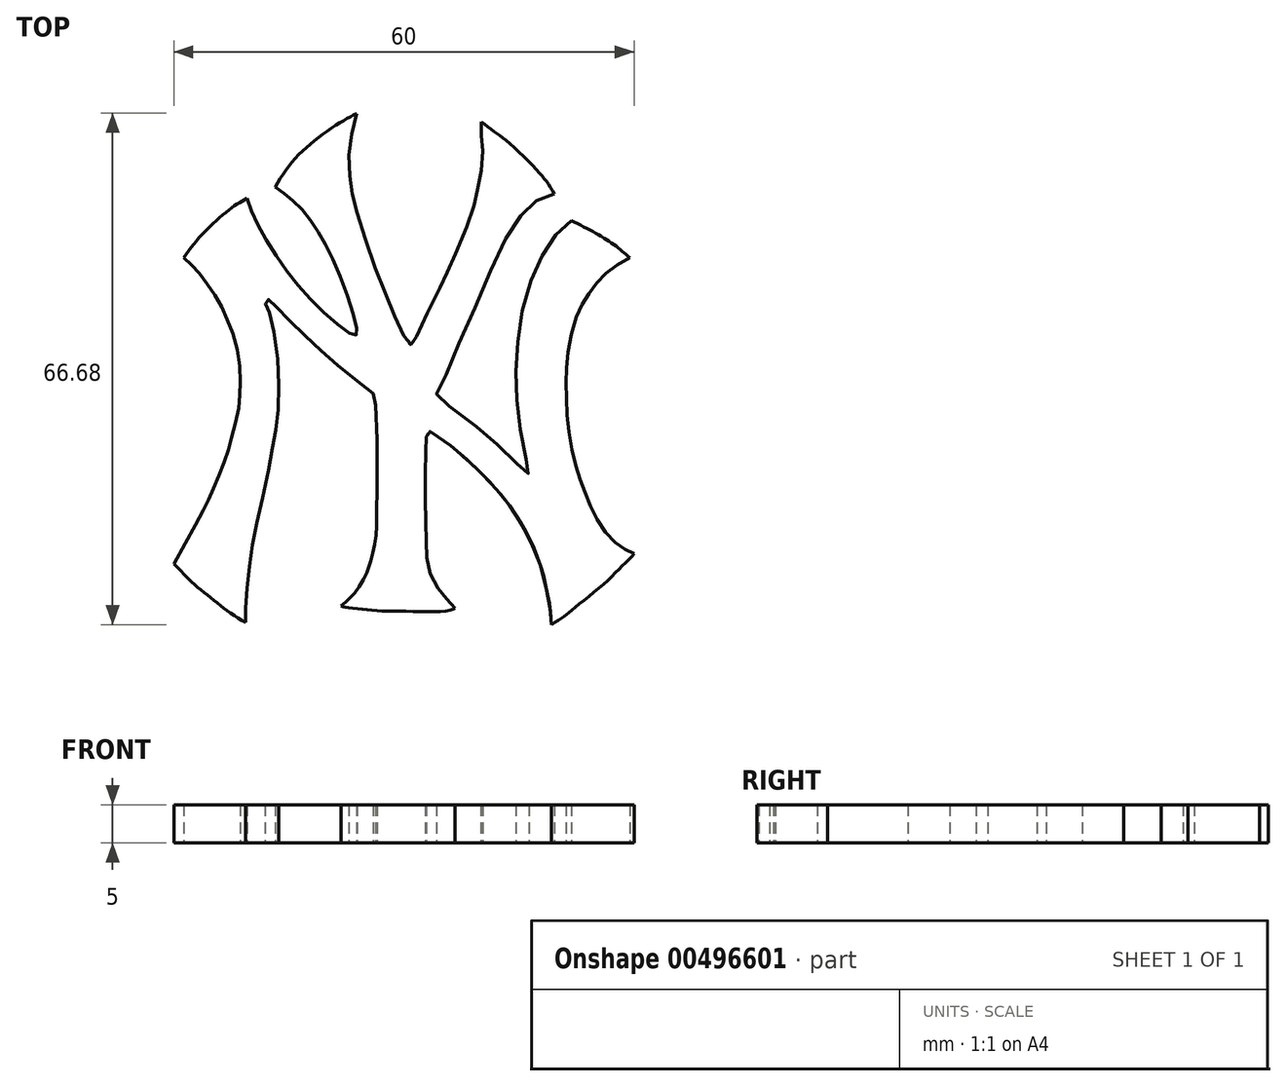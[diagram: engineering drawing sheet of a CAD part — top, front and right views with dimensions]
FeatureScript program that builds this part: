
annotation { "Feature Type Name" : "Feature", "Feature Type Description" : "" }
export const myFeature = defineFeature(function(context is Context, id is Id, definition is map)
    precondition{}
    {
        {
            var Q0;
            Q0=qCreatedBy(makeId("Top.planeOp"),FACE);
            var sketch = newSketch(context, id + "F0", { "sketchPlane" : qUnion([Q0])});
            skFitSpline(sketch, "E0", {"points": [v(-20.6, 24.51) * mm, v(-21.8, 23.88) * mm, v(-23.3, 22.78) * mm, v(-25.43, 20.88) * mm, v(-27.16, 19.06) * mm, v(-28.9, 16.77) * mm], "startDerivative": vector(-7.62, -3.74) * mm, "endDerivative": vector(-7.65, -10.58) * mm});
            skFitSpline(sketch, "E1", {"points": [v(-28.9, 16.77) * mm, v(-27.48, 15.5) * mm, v(-25.98, 13.53) * mm, v(-24.24, 11) * mm, v(-22.98, 8.16) * mm, v(-21.71, 3.97) * mm, v(-21.55, 0) * mm, v(-21.71, -2.67) * mm, v(-22.58, -6.46) * mm, v(-23.21, -8.83) * mm, v(-24.48, -12) * mm, v(-25.5, -14.44) * mm, v(-26.7, -16.81) * mm, v(-30.17, -23.14) * mm], "startDerivative": vector(24.88, -19.82) * mm, "endDerivative": vector(-34.53, -62.2) * mm});
            skFitSpline(sketch, "E2", {"points": [v(-30.17, -23.14) * mm, v(-28.9, -24.47) * mm, v(-27.36, -25.97) * mm, v(-25.27, -27.63) * mm, v(-23.21, -29.25) * mm, v(-20.84, -30.8) * mm], "startDerivative": vector(7.12, -7.55) * mm, "endDerivative": vector(11.27, -6.93) * mm});
            skFitSpline(sketch, "E3", {"points": [v(-20.84, -30.8) * mm, v(-20.84, -28.86) * mm, v(-20.49, -25.02) * mm, v(-19.93, -20.68) * mm, v(-18.87, -15.74) * mm, v(-17.52, -9.22) * mm, v(-16.96, -6.01) * mm, v(-16.51, -1.88) * mm, v(-16.74, 4.38) * mm, v(-17.63, 9.4) * mm, v(-18.07, 10.37) * mm, v(-18.27, 11.01) * mm, v(-18.07, 11.35) * mm, v(-17.68, 11.27) * mm, v(-16.9, 10.43) * mm, v(-14.53, 8) * mm, v(-11.31, 4.92) * mm, v(-7.93, 2.02) * mm, v(-4.22, -0.92) * mm], "startDerivative": vector(-1.2, 39.83) * mm, "endDerivative": vector(54.21, -42.15) * mm});
            skFitSpline(sketch, "E4", {"points": [v(-4.22, -0.92) * mm, v(-3.85, -2.48) * mm], "startDerivative": vector(0.36, -1.56) * mm, "endDerivative": vector(0.36, -1.56) * mm});
            skFitSpline(sketch, "E5", {"points": [v(-3.85, -2.48) * mm, v(-3.66, -8.07) * mm, v(-3.7, -15) * mm, v(-3.72, -16.94) * mm, v(-3.85, -19.64) * mm, v(-4.5, -22.63) * mm, v(-4.94, -24.05) * mm, v(-6.07, -26.2) * mm, v(-7.38, -27.78) * mm, v(-8.37, -28.62) * mm], "startDerivative": vector(1.65, -32.98) * mm, "endDerivative": vector(-12.84, -10.3) * mm});
            skFitSpline(sketch, "E6", {"points": [v(-8.37, -28.62) * mm, v(-7.9, -28.81) * mm, v(-6.02, -29) * mm, v(-3.29, -29.27) * mm, v(0.79, -29.34) * mm, v(5.5, -29.26) * mm, v(6.51, -28.9) * mm], "startDerivative": vector(4.84, -2.6) * mm, "endDerivative": vector(6.8, 3.5) * mm});
            skFitSpline(sketch, "E7", {"points": [v(6.51, -28.9) * mm, v(5.6, -27.93) * mm, v(4.49, -26.66) * mm, v(3.35, -24.62) * mm, v(2.78, -22.22) * mm, v(2.73, -19.85) * mm, v(2.64, -16.02) * mm, v(2.64, -10.53) * mm, v(2.73, -7.14) * mm, v(2.84, -6.23) * mm, v(3.05, -5.91) * mm, v(3.4, -5.92) * mm, v(4.07, -6.44) * mm, v(5.65, -7.56) * mm, v(8.76, -10.22) * mm, v(11.63, -13.12) * mm, v(13.92, -16.04) * mm, v(16.13, -19.75) * mm, v(17.87, -24.18) * mm, v(18.82, -28.62) * mm, v(19.08, -31.06) * mm], "startDerivative": vector(-24.2, 26.34) * mm, "endDerivative": vector(3.79, -45.4) * mm});
            skFitSpline(sketch, "E8", {"points": [v(19.08, -31.06) * mm, v(20.64, -30.08) * mm, v(21.79, -29.13) * mm, v(25.36, -26.22) * mm, v(28.14, -23.58) * mm, v(29.83, -21.85) * mm], "startDerivative": vector(10.32, 6.05) * mm, "endDerivative": vector(8.55, 8.85) * mm});
            skFitSpline(sketch, "E9", {"points": [v(29.83, -21.85) * mm, v(28, -20.81) * mm, v(25.55, -18.27) * mm, v(23.67, -14.37) * mm, v(22.44, -11) * mm, v(21.3, -5.78) * mm, v(20.98, -0.57) * mm, v(21.14, 3.66) * mm, v(22.4, 9.31) * mm, v(23.98, 12.12) * mm, v(26.1, 14.72) * mm, v(29.3, 16.77) * mm], "startDerivative": vector(-27.08, 13.1) * mm, "endDerivative": vector(38.6, 20.7) * mm});
            skFitSpline(sketch, "E10", {"points": [v(29.3, 16.77) * mm, v(26.5, 18.98) * mm, v(21.65, 21.64) * mm], "startDerivative": vector(-5.75, 5) * mm, "endDerivative": vector(-9.43, 4.75) * mm});
            skFitSpline(sketch, "E11", {"points": [v(21.65, 21.64) * mm, v(20.18, 20.38) * mm, v(18.52, 18.19) * mm, v(17.1, 15.5) * mm, v(15.7, 11.64) * mm, v(14.8, 7.06) * mm, v(14.44, 2.77) * mm, v(14.5, -0.92) * mm, v(14.9, -4.82) * mm, v(15.7, -9.28) * mm, v(16.1, -10.8) * mm, v(16.08, -11.33) * mm, v(15.63, -11.3) * mm, v(14.67, -10.2) * mm, v(12.25, -7.8) * mm, v(9.76, -5.66) * mm, v(5.62, -2.48) * mm, v(4.14, -1.25) * mm, v(4.1, -0.92) * mm, v(5.01, 0.94) * mm, v(7, 5.6) * mm, v(9.88, 12.12) * mm, v(12.56, 18.3) * mm, v(14.62, 21.64) * mm, v(16.32, 23.6) * mm, v(17.78, 24.58) * mm, v(19.44, 25.13) * mm], "startDerivative": vector(-46.4, -35.94) * mm, "endDerivative": vector(56.95, 15.73) * mm});
            skFitSpline(sketch, "E12", {"points": [v(19.44, 25.13) * mm, v(18.42, 26.71) * mm, v(16.98, 28.4) * mm, v(13.34, 31.95) * mm, v(11.7, 33.18) * mm, v(9.9, 34.49) * mm], "startDerivative": vector(-5.86, 9.59) * mm, "endDerivative": vector(-10.1, 7.52) * mm});
            skFitSpline(sketch, "E13", {"points": [v(9.9, 34.49) * mm, v(9.9, 32.59) * mm, v(10.08, 29.67) * mm, v(9.38, 25.47) * mm, v(8.7, 22.65) * mm, v(5.86, 15.8) * mm, v(4.7, 13.28) * mm, v(1.44, 6.53) * mm, v(0.85, 5.52) * mm, v(0.46, 5.6) * mm, v(-1.1, 8.6) * mm, v(-3.72, 14.91) * mm, v(-6.41, 23.04) * mm, v(-7.14, 26.59) * mm, v(-7.28, 31.03) * mm, v(-6.37, 35.62) * mm], "startDerivative": vector(-1.6, -38.96) * mm, "endDerivative": vector(15.71, 61.1) * mm});
            skFitSpline(sketch, "E14", {"points": [v(-6.37, 35.62) * mm, v(-8.37, 34.49) * mm, v(-11.7, 32.15) * mm, v(-14.77, 29.25) * mm, v(-16.95, 26) * mm], "startDerivative": vector(-9.36, -5) * mm, "endDerivative": vector(-7.7, -12.78) * mm});
            skFitSpline(sketch, "E15", {"points": [v(-16.95, 26) * mm, v(-15.11, 24.6) * mm, v(-12.88, 22.37) * mm, v(-10.8, 19.19) * mm, v(-8.37, 14.05) * mm, v(-6.37, 7.73) * mm, v(-6.37, 6.73) * mm, v(-7.28, 6.95) * mm, v(-11.53, 10.53) * mm, v(-15.67, 15.39) * mm, v(-19.19, 20.98) * mm, v(-20.6, 24.51) * mm], "startDerivative": vector(25.67, -18.42) * mm, "endDerivative": vector(-12.62, 36.95) * mm});
            skSolve(sketch);
        }
        {
            var Q0;
            Q0 = qSketchRegion(id + "F0", true);
            extrude(context, id + "F1", {"entities" : qUnion([Q0]), "depth" : 5 * mm, "offsetDistance" : 25 * mm});
        }
    });
